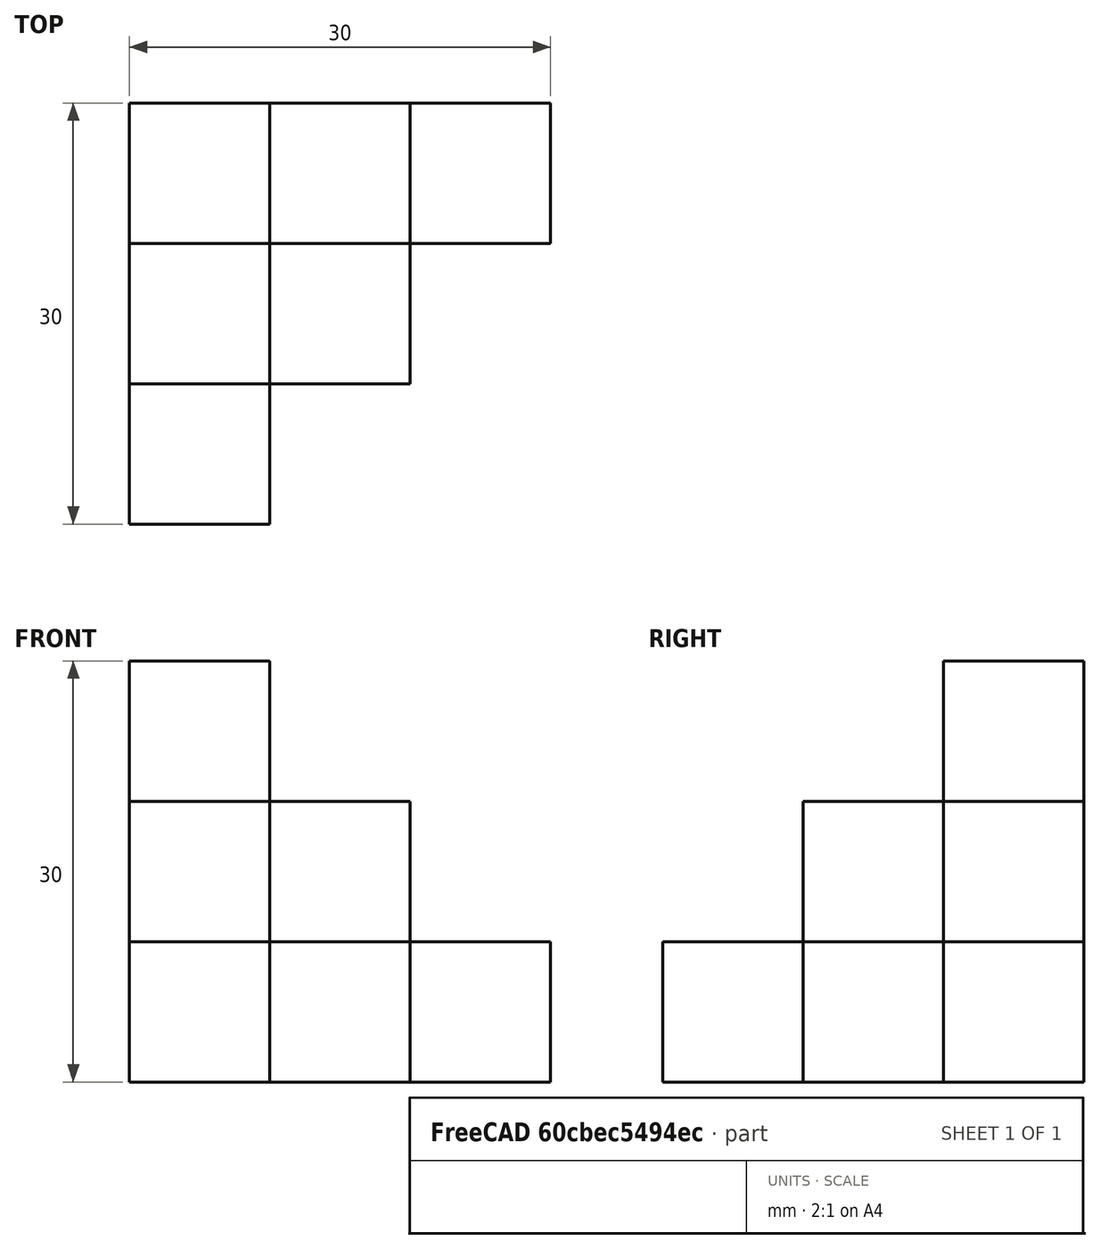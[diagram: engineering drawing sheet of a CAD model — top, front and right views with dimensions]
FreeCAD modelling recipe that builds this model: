
FCSTD DOCUMENT  (FreeCAD 0.21R33771 (Git))
Label: PrimeraFigura
License: All rights reserved
LicenseURL: http://en.wikipedia.org/wiki/All_rights_reserved
objects: Part::Box×6, App::DocumentObjectGroup×1, Part::FeaturePython×1
note: 7 computed .brp shape members not serialized (recipe doc carries the construction recipe); baked Part::Feature solids carry a one-line shape summary decoded from their .brp

FEATURE [Part::Box] Box005  label="Cubo005"
  AttacherType = Attacher::AttachEngine3D
  Height = 10
  Length = 10
  Placement = pos=(10,-10,0) rot=(0,0,1;0rad)
  Width = 10
FEATURE [Part::Box] Box004  label="Cubo004"
  AttacherType = Attacher::AttachEngine3D
  Height = 10
  Length = 10
  Placement = pos=(0,-20,0) rot=(0,0,1;0rad)
  Width = 10
FEATURE [Part::Box] Box003  label="Cubo003"
  AttacherType = Attacher::AttachEngine3D
  Height = 20
  Length = 10
  Placement = pos=(0,-10,0) rot=(0,0,1;0rad)
  Width = 10
FEATURE [Part::Box] Box002  label="Cubo002"
  AttacherType = Attacher::AttachEngine3D
  Height = 10
  Length = 10
  Placement = pos=(20,0,0) rot=(0,0,1;0rad)
  Width = 10
FEATURE [Part::Box] Box001  label="Cubo001"
  AttacherType = Attacher::AttachEngine3D
  Height = 20
  Length = 10
  Placement = pos=(10,0,0) rot=(0,0,1;0rad)
  Width = 10
FEATURE [Part::Box] Box  label="Cubo"
  AttacherType = Attacher::AttachEngine3D
  Height = 30
  Length = 10
  Width = 10
FEATURE [App::DocumentObjectGroup] Group  label="Grupo"
  Group = -> [Box,Box001,Box002,Box003,Box004,Box005]
FEATURE [Part::FeaturePython] Connect  # WARN: FeaturePython — macro-defined, semantics opaque (R4)
  Objects = -> [Box005,Box,Box001,Box002,Box003,Box004]
  Refine = true
  Tolerance = 0
